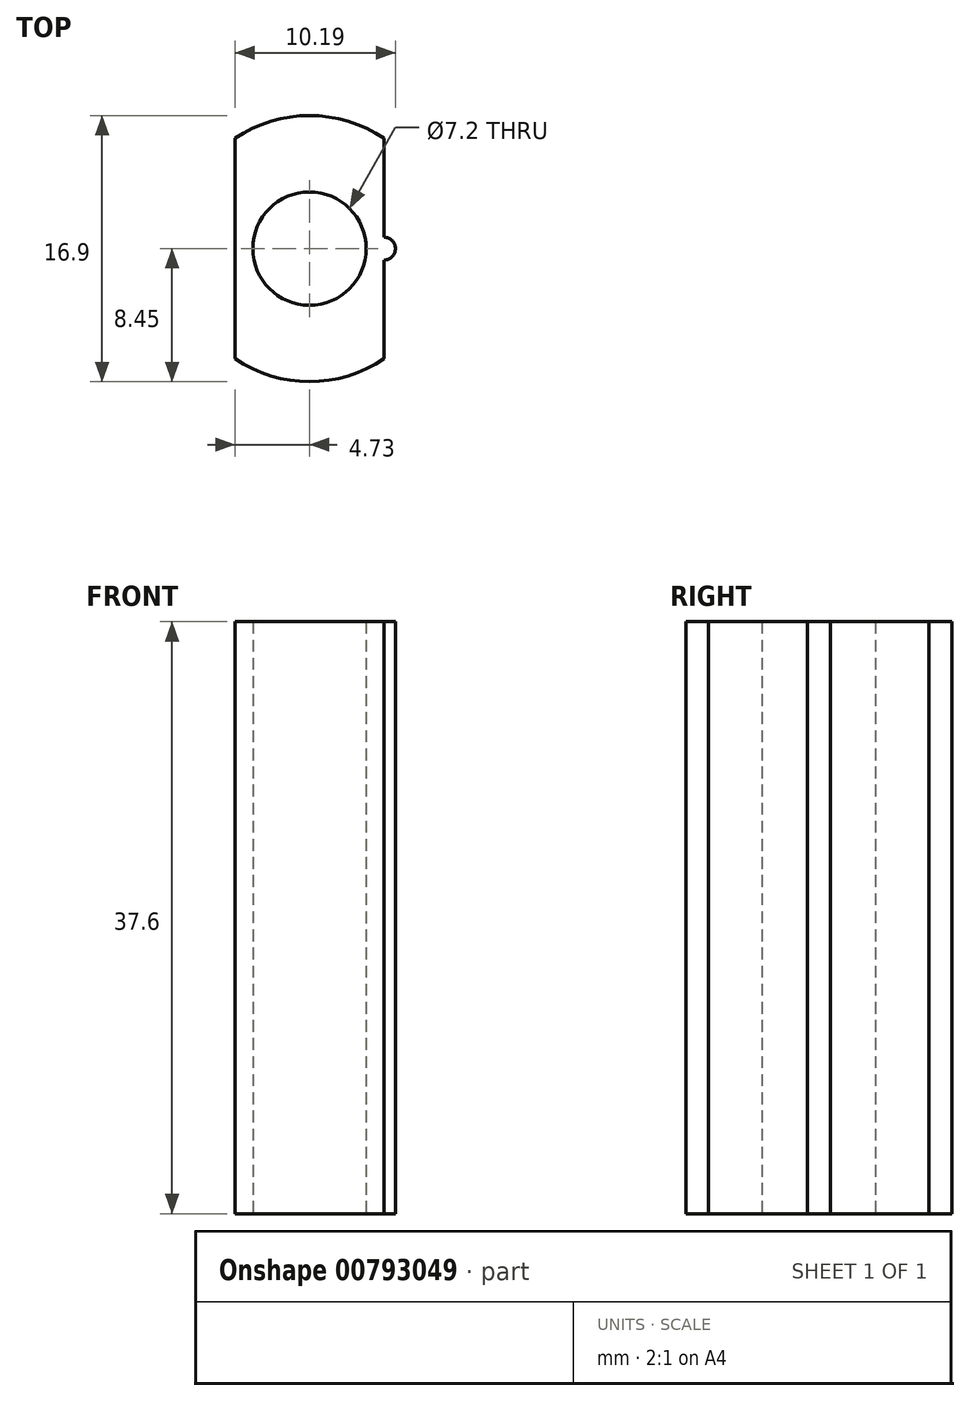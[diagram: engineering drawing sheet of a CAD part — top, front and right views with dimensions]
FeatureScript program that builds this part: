
annotation { "Feature Type Name" : "Feature", "Feature Type Description" : "" }
export const myFeature = defineFeature(function(context is Context, id is Id, definition is map)
    precondition{}
    {
        {
            var Q0;
            Q0=qCreatedBy(makeId("Top.planeOp"),FACE);
            var sketch = newSketch(context, id + "F0", { "sketchPlane" : qUnion([Q0])});
            skCircle(sketch, "E0", {"center": v(0, 0) * mm, "radius": 2.25 * mm});
            skCircle(sketch, "E1", {"center": v(0, 0) * mm, "radius": 3.6 * mm});
            skCircle(sketch, "E2", {"center": v(0, 0) * mm, "radius": 8.45 * mm});
            skPoint(sketch, "E3.third.point", {"position": v(0, 8.45) * mm});
            skLineSegment(sketch, "E4", {"start": v(-4.73, 7) * mm, "end": v(-4.73, -7) * mm});
            skLineSegment(sketch, "E5", {"start": v(4.73, 7) * mm, "end": v(4.73, -7) * mm});
            skSolve(sketch);
        }
        {
            var Q0;
            Q0=makeQuery(id+"F0.imprint","IMPRINT",FACE,{"disambiguationData":[TD([[makeQuery(id+"F0.imprint","IMPRINT",EDGE,{"derivedFrom":sQuery(id+"F0.wireOp",EDGE,"E1")}),-1.0]])]});
            extrude(context, id + "F1", {"entities" : qUnion([Q0]), "depth" : 37.6 * mm, "offsetDistance" : 25 * mm});
        }
        {
            var Q0;
            Q0=makeQuery(id+"F1.opExtrude","CAP_FACE",FACE,{"disambiguationData":[OSD([sQuery(id+"F0.wireOp",EDGE,"E1"),sQuery(id+"F0.wireOp",EDGE,"E2"),sQuery(id+"F0.wireOp",EDGE,"KH23BS3D-JL4F-74Ev-Pb4K-CxiVbHcmElIK"),sQuery(id+"F0.wireOp",EDGE,"zq3N2CP0-ENyl-08Kw-hhLl-wFrkG8kHy9t0")])],"isStart":false});
            var sketch = newSketch(context, id + "F2", { "sketchPlane" : qUnion([Q0])});
            skCircle(sketch, "E6", {"center": v(4.73, 0) * mm, "radius": 0.72 * mm});
            skSolve(sketch);
        }
        {
            var Q0;
            Q0 = qSketchRegion(id + "F2", true);
            extrude(context, id + "F3", {"entities" : qUnion([Q0]), "operationType" : NewBodyOperationType.ADD, "oppositeDirection" : true, "depth" : 37.6 * mm, "offsetDistance" : 25 * mm});
        }
    });
